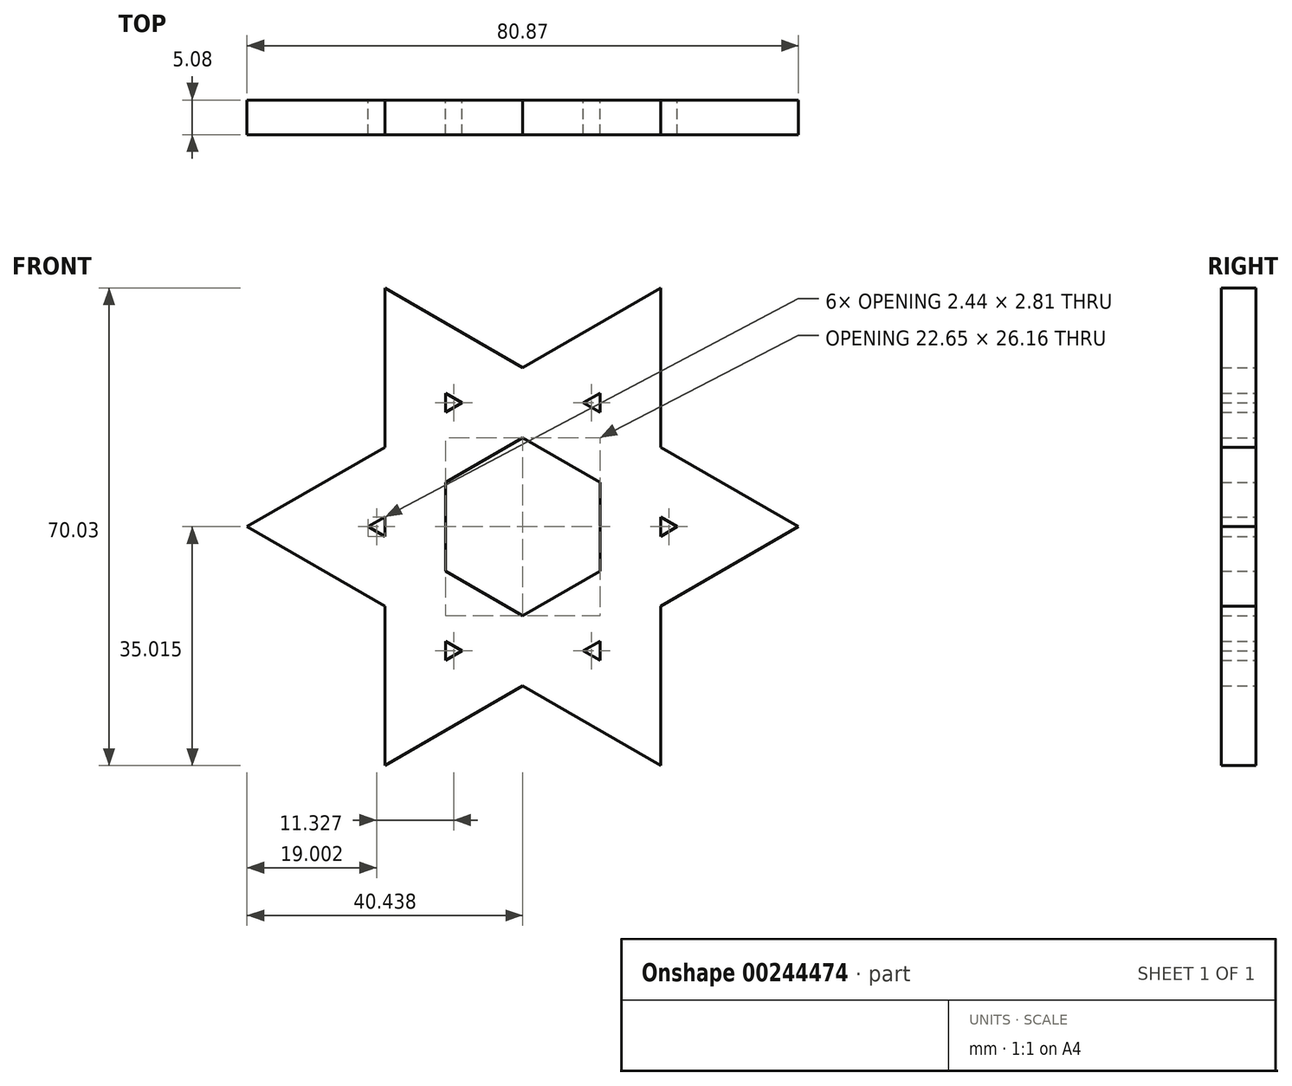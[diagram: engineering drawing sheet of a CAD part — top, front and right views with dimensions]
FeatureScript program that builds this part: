
annotation { "Feature Type Name" : "Feature", "Feature Type Description" : "" }
export const myFeature = defineFeature(function(context is Context, id is Id, definition is map)
    precondition{}
    {
        {
            var Q0;
            Q0=qCreatedBy(makeId("Front.planeOp"),FACE);
            var sketch = newSketch(context, id + "F0", { "sketchPlane" : qUnion([Q0])});
            skPoint(sketch, "E0.0.midPoint", {"position": v(-0.44, 25.15) * mm});
            skLineSegment(sketch, "E1", {"start": v(-0.44, 25.15) * mm, "end": v(-7.77, 12.45) * mm});
            skLineSegment(sketch, "E2", {"start": v(-22.21, -12.56) * mm, "end": v(-7.77, -12.7) * mm});
            skLineSegment(sketch, "E3", {"start": v(21.56, -12.95) * mm, "end": v(14.22, -0.25) * mm});
            skLineSegment(sketch, "E4", {"start": v(21.26, 12.45) * mm, "end": v(6.75, 12.45) * mm});
            skLineSegment(sketch, "E5", {"start": v(-22.44, 12.45) * mm, "end": v(-15.1, -0.25) * mm});
            skLineSegment(sketch, "E6", {"start": v(-0.59, -25.4) * mm, "end": v(6.75, -12.7) * mm});
            skLineSegment(sketch, "E7", {"start": v(-7.77, 12.45) * mm, "end": v(-15, -0.06) * mm});
            skLineSegment(sketch, "E8", {"start": v(-7.77, 12.45) * mm, "end": v(-22.44, 12.45) * mm});
            skLineSegment(sketch, "E9", {"start": v(-15, -0.06) * mm, "end": v(-22.21, -12.56) * mm});
            skLineSegment(sketch, "E10", {"start": v(-15.1, -0.25) * mm, "end": v(-7.85, -12.83) * mm});
            skLineSegment(sketch, "E11", {"start": v(6.75, 12.45) * mm, "end": v(-7.77, 12.45) * mm});
            skLineSegment(sketch, "E12", {"start": v(6.9, 12.45) * mm, "end": v(-0.44, 25.15) * mm});
            skLineSegment(sketch, "E13", {"start": v(14.22, -0.25) * mm, "end": v(6.9, 12.45) * mm});
            skLineSegment(sketch, "E14", {"start": v(14.08, 0) * mm, "end": v(21.26, 12.45) * mm});
            skLineSegment(sketch, "E15", {"start": v(6.75, -12.7) * mm, "end": v(14.08, 0) * mm});
            skLineSegment(sketch, "E16", {"start": v(6.68, -12.82) * mm, "end": v(21.56, -12.95) * mm});
            skLineSegment(sketch, "E17", {"start": v(-7.85, -12.83) * mm, "end": v(-0.59, -25.4) * mm});
            skLineSegment(sketch, "E18", {"start": v(-7.77, -12.7) * mm, "end": v(6.68, -12.82) * mm});
            skLineSegment(sketch, "E19.0", {"start": v(20.22, 95.25) * mm, "end": v(20.22, 71.9) * mm});
            skLineSegment(sketch, "E19.1", {"start": v(20.22, 25.21) * mm, "end": v(0, 36.89) * mm});
            skLineSegment(sketch, "E19.2", {"start": v(-40.43, 60.23) * mm, "end": v(-20.22, 71.9) * mm});
            skPoint(sketch, "E19.0.midPoint", {"position": v(20.22, 60.23) * mm});
            skCircle(sketch, "E20.cCircle", {"center": v(0, 60.23) * mm, "radius": 20.22 * mm, "construction": true});
            skLineSegment(sketch, "E20.0", {"start": v(-20.22, 25.21) * mm, "end": v(-20.22, 48.56) * mm});
            skLineSegment(sketch, "E20.1", {"start": v(-20.22, 95.25) * mm, "end": v(0, 83.57) * mm});
            skLineSegment(sketch, "E20.2", {"start": v(40.43, 60.23) * mm, "end": v(20.22, 48.56) * mm});
            skPoint(sketch, "E20.0.midPoint", {"position": v(-20.22, 60.23) * mm});
            skLineSegment(sketch, "E21", {"start": v(8.9, 78.44) * mm, "end": v(20.22, 71.9) * mm});
            skLineSegment(sketch, "E22", {"start": v(0, 83.57) * mm, "end": v(20.22, 95.25) * mm});
            skLineSegment(sketch, "E23", {"start": v(20.22, 71.9) * mm, "end": v(40.43, 60.23) * mm});
            skLineSegment(sketch, "E24", {"start": v(20.22, 61.64) * mm, "end": v(20.22, 48.56) * mm});
            skLineSegment(sketch, "E25", {"start": v(20.22, 48.56) * mm, "end": v(20.22, 25.21) * mm});
            skLineSegment(sketch, "E26", {"start": v(11.33, 43.43) * mm, "end": v(0, 36.89) * mm});
            skLineSegment(sketch, "E27", {"start": v(0, 36.89) * mm, "end": v(-20.22, 25.21) * mm});
            skLineSegment(sketch, "E28", {"start": v(-8.9, 42.02) * mm, "end": v(-20.22, 48.56) * mm});
            skLineSegment(sketch, "E29", {"start": v(-20.22, 48.56) * mm, "end": v(-40.43, 60.23) * mm});
            skLineSegment(sketch, "E30", {"start": v(-20.22, 58.82) * mm, "end": v(-20.22, 71.9) * mm});
            skLineSegment(sketch, "E31", {"start": v(-20.22, 71.9) * mm, "end": v(-20.22, 95.25) * mm});
            skLineSegment(sketch, "E32", {"start": v(-11.33, 77.04) * mm, "end": v(0, 83.57) * mm});
            skLineSegment(sketch, "E33.0", {"start": v(-11.33, 53.7) * mm, "end": v(-11.33, 66.77) * mm});
            skLineSegment(sketch, "E33.1", {"start": v(0, 73.3) * mm, "end": v(11.33, 66.77) * mm});
            skLineSegment(sketch, "E33.2", {"start": v(11.33, 66.77) * mm, "end": v(11.33, 53.7) * mm});
            skLineSegment(sketch, "E33.3", {"start": v(-11.33, 66.77) * mm, "end": v(0, 73.3) * mm});
            skLineSegment(sketch, "E33.4", {"start": v(11.33, 53.7) * mm, "end": v(0, 47.15) * mm});
            skLineSegment(sketch, "E33.5", {"start": v(0, 47.15) * mm, "end": v(-11.33, 53.7) * mm});
            skLineSegment(sketch, "E34", {"start": v(-8.84, 78.41) * mm, "end": v(-11.33, 79.85) * mm});
            skLineSegment(sketch, "E35", {"start": v(-11.33, 66.77) * mm, "end": v(-11.33, 79.85) * mm});
            skLineSegment(sketch, "E36", {"start": v(11.33, 66.77) * mm, "end": v(22.65, 60.23) * mm});
            skLineSegment(sketch, "E37", {"start": v(20.17, 58.8) * mm, "end": v(22.65, 60.23) * mm});
            skLineSegment(sketch, "E38", {"start": v(-20.17, 61.67) * mm, "end": v(-22.65, 60.23) * mm});
            skLineSegment(sketch, "E39", {"start": v(-11.33, 53.7) * mm, "end": v(-22.65, 60.23) * mm});
            skLineSegment(sketch, "E40", {"start": v(-11.33, 43.48) * mm, "end": v(-11.33, 40.61) * mm});
            skLineSegment(sketch, "E41", {"start": v(0, 47.15) * mm, "end": v(-11.33, 40.61) * mm});
            skLineSegment(sketch, "E42", {"start": v(8.84, 42.05) * mm, "end": v(11.33, 40.61) * mm});
            skLineSegment(sketch, "E43", {"start": v(11.33, 53.7) * mm, "end": v(11.33, 40.61) * mm});
            skLineSegment(sketch, "E44", {"start": v(0, 73.3) * mm, "end": v(11.33, 79.85) * mm});
            skLineSegment(sketch, "E45", {"start": v(11.33, 76.98) * mm, "end": v(11.33, 79.85) * mm});
            skPoint(sketch, "E46.orphan", {"position": v(15.26, 82.12) * mm});
            skPoint(sketch, "E47.orphan", {"position": v(-15.26, 82.12) * mm});
            skLineSegment(sketch, "E48.0", {"start": v(143.19, 1.7) * mm, "end": v(143.19, -21.64) * mm});
            skLineSegment(sketch, "E48.1", {"start": v(143.19, -68.33) * mm, "end": v(122.97, -56.66) * mm});
            skLineSegment(sketch, "E48.2", {"start": v(82.53, -33.31) * mm, "end": v(102.75, -21.64) * mm});
            skPoint(sketch, "E48.0.midPoint", {"position": v(143.19, -33.31) * mm});
            skCircle(sketch, "E49.cCircle", {"center": v(122.97, -33.31) * mm, "radius": 20.22 * mm, "construction": true});
            skLineSegment(sketch, "E49.0", {"start": v(102.75, -68.33) * mm, "end": v(102.75, -44.99) * mm});
            skLineSegment(sketch, "E49.1", {"start": v(102.75, 1.7) * mm, "end": v(122.97, -9.97) * mm});
            skLineSegment(sketch, "E49.2", {"start": v(163.4, -33.31) * mm, "end": v(143.19, -44.99) * mm});
            skPoint(sketch, "E49.0.midPoint", {"position": v(102.75, -33.31) * mm});
            skLineSegment(sketch, "E50", {"start": v(131.86, -15.1) * mm, "end": v(134.3, -16.5) * mm});
            skLineSegment(sketch, "E51", {"start": v(122.97, -9.97) * mm, "end": v(143.19, 1.7) * mm});
            skLineSegment(sketch, "E52", {"start": v(143.19, -21.64) * mm, "end": v(163.4, -33.31) * mm});
            skLineSegment(sketch, "E53", {"start": v(143.19, -31.9) * mm, "end": v(143.19, -34.72) * mm});
            skLineSegment(sketch, "E54", {"start": v(143.19, -44.99) * mm, "end": v(143.19, -68.33) * mm});
            skLineSegment(sketch, "E55", {"start": v(134.3, -50.12) * mm, "end": v(122.97, -56.66) * mm});
            skLineSegment(sketch, "E56", {"start": v(122.97, -56.66) * mm, "end": v(102.75, -68.33) * mm});
            skLineSegment(sketch, "E57", {"start": v(114.08, -51.53) * mm, "end": v(111.64, -50.12) * mm});
            skLineSegment(sketch, "E58", {"start": v(102.75, -44.99) * mm, "end": v(82.53, -33.31) * mm});
            skLineSegment(sketch, "E59", {"start": v(102.75, -34.72) * mm, "end": v(102.75, -31.9) * mm});
            skLineSegment(sketch, "E60", {"start": v(102.75, -21.64) * mm, "end": v(102.75, 1.7) * mm});
            skLineSegment(sketch, "E61", {"start": v(111.64, -16.5) * mm, "end": v(114.08, -15.1) * mm});
            skLineSegment(sketch, "E62.0", {"start": v(111.64, -39.85) * mm, "end": v(111.64, -26.77) * mm});
            skLineSegment(sketch, "E62.1", {"start": v(122.97, -20.24) * mm, "end": v(134.3, -26.77) * mm});
            skLineSegment(sketch, "E62.2", {"start": v(134.3, -26.77) * mm, "end": v(134.3, -39.85) * mm});
            skLineSegment(sketch, "E62.3", {"start": v(111.64, -26.77) * mm, "end": v(122.97, -20.24) * mm});
            skLineSegment(sketch, "E62.4", {"start": v(134.3, -39.85) * mm, "end": v(122.97, -46.4) * mm});
            skLineSegment(sketch, "E62.5", {"start": v(122.97, -46.4) * mm, "end": v(111.64, -39.85) * mm});
            skLineSegment(sketch, "E63", {"start": v(114.13, -15.13) * mm, "end": v(111.64, -13.7) * mm});
            skLineSegment(sketch, "E64", {"start": v(111.64, -16.57) * mm, "end": v(111.64, -13.7) * mm});
            skLineSegment(sketch, "E65", {"start": v(143.13, -31.88) * mm, "end": v(145.62, -33.31) * mm});
            skLineSegment(sketch, "E66", {"start": v(143.13, -34.75) * mm, "end": v(145.62, -33.31) * mm});
            skLineSegment(sketch, "E67", {"start": v(102.8, -31.88) * mm, "end": v(100.31, -33.31) * mm});
            skLineSegment(sketch, "E68", {"start": v(102.8, -34.75) * mm, "end": v(100.31, -33.31) * mm});
            skLineSegment(sketch, "E69", {"start": v(111.64, -50.06) * mm, "end": v(111.64, -52.93) * mm});
            skLineSegment(sketch, "E70", {"start": v(114.13, -51.5) * mm, "end": v(111.64, -52.93) * mm});
            skLineSegment(sketch, "E71", {"start": v(131.8, -51.5) * mm, "end": v(134.3, -52.93) * mm});
            skLineSegment(sketch, "E72", {"start": v(134.3, -50.06) * mm, "end": v(134.3, -52.93) * mm});
            skLineSegment(sketch, "E73", {"start": v(131.8, -15.13) * mm, "end": v(134.3, -13.7) * mm});
            skLineSegment(sketch, "E74", {"start": v(134.3, -16.57) * mm, "end": v(134.3, -13.7) * mm});
            skPoint(sketch, "E75.orphan", {"position": v(138.23, -11.42) * mm});
            skPoint(sketch, "E76.orphan", {"position": v(107.7, -11.42) * mm});
            skLineSegment(sketch, "E77.0", {"start": v(-108.48, 41.43) * mm, "end": v(-108.48, 18.09) * mm});
            skLineSegment(sketch, "E77.1", {"start": v(-108.48, -28.6) * mm, "end": v(-128.7, -16.93) * mm});
            skLineSegment(sketch, "E77.2", {"start": v(-169.14, 6.41) * mm, "end": v(-148.92, 18.09) * mm});
            skPoint(sketch, "E77.0.midPoint", {"position": v(-108.48, 6.41) * mm});
            skCircle(sketch, "E78.cCircle", {"center": v(-128.7, 6.41) * mm, "radius": 20.22 * mm, "construction": true});
            skLineSegment(sketch, "E78.0", {"start": v(-148.92, -28.6) * mm, "end": v(-148.92, -5.26) * mm});
            skLineSegment(sketch, "E78.1", {"start": v(-148.92, 41.43) * mm, "end": v(-128.7, 29.76) * mm});
            skLineSegment(sketch, "E78.2", {"start": v(-88.27, 6.41) * mm, "end": v(-108.48, -5.26) * mm});
            skPoint(sketch, "E78.0.midPoint", {"position": v(-148.92, 6.41) * mm});
            skLineSegment(sketch, "E79", {"start": v(-119.81, 24.63) * mm, "end": v(-108.48, 18.09) * mm});
            skLineSegment(sketch, "E80", {"start": v(-128.7, 29.76) * mm, "end": v(-108.48, 41.43) * mm});
            skLineSegment(sketch, "E81", {"start": v(-108.48, 18.09) * mm, "end": v(-88.27, 6.41) * mm});
            skLineSegment(sketch, "E82", {"start": v(-108.48, 7.82) * mm, "end": v(-108.48, -5.26) * mm});
            skLineSegment(sketch, "E83", {"start": v(-108.48, -5.26) * mm, "end": v(-108.48, -28.6) * mm});
            skLineSegment(sketch, "E84", {"start": v(-117.37, -10.4) * mm, "end": v(-128.7, -16.93) * mm});
            skLineSegment(sketch, "E85", {"start": v(-128.7, -16.93) * mm, "end": v(-148.92, -28.6) * mm});
            skLineSegment(sketch, "E86", {"start": v(-137.6, -11.8) * mm, "end": v(-148.92, -5.26) * mm});
            skLineSegment(sketch, "E87", {"start": v(-148.92, -5.26) * mm, "end": v(-169.14, 6.41) * mm});
            skLineSegment(sketch, "E88", {"start": v(-148.92, 5) * mm, "end": v(-148.92, 18.09) * mm});
            skLineSegment(sketch, "E89", {"start": v(-148.92, 18.09) * mm, "end": v(-148.92, 41.43) * mm});
            skLineSegment(sketch, "E90", {"start": v(-140.03, 23.22) * mm, "end": v(-128.7, 29.76) * mm});
            skLineSegment(sketch, "E91.0", {"start": v(-140.03, -0.13) * mm, "end": v(-140.03, 12.95) * mm});
            skLineSegment(sketch, "E91.1", {"start": v(-128.7, 19.5) * mm, "end": v(-117.37, 12.95) * mm});
            skLineSegment(sketch, "E91.2", {"start": v(-117.37, 12.95) * mm, "end": v(-117.37, -0.13) * mm});
            skLineSegment(sketch, "E91.3", {"start": v(-140.03, 12.95) * mm, "end": v(-128.7, 19.5) * mm});
            skLineSegment(sketch, "E91.4", {"start": v(-117.37, -0.13) * mm, "end": v(-128.7, -6.67) * mm});
            skLineSegment(sketch, "E91.5", {"start": v(-128.7, -6.67) * mm, "end": v(-140.03, -0.13) * mm});
            skLineSegment(sketch, "E92", {"start": v(-137.54, 24.6) * mm, "end": v(-140.03, 26.03) * mm});
            skLineSegment(sketch, "E93", {"start": v(-140.03, 12.95) * mm, "end": v(-140.03, 26.03) * mm});
            skLineSegment(sketch, "E94", {"start": v(-117.37, 12.95) * mm, "end": v(-106.05, 6.41) * mm});
            skLineSegment(sketch, "E95", {"start": v(-108.54, 4.98) * mm, "end": v(-106.05, 6.41) * mm});
            skLineSegment(sketch, "E96", {"start": v(-148.87, 7.85) * mm, "end": v(-151.36, 6.41) * mm});
            skLineSegment(sketch, "E97", {"start": v(-140.03, -0.13) * mm, "end": v(-151.36, 6.41) * mm});
            skLineSegment(sketch, "E98", {"start": v(-140.03, -10.33) * mm, "end": v(-140.03, -13.2) * mm});
            skLineSegment(sketch, "E99", {"start": v(-128.7, -6.67) * mm, "end": v(-140.03, -13.2) * mm});
            skLineSegment(sketch, "E100", {"start": v(-119.86, -11.77) * mm, "end": v(-117.37, -13.2) * mm});
            skLineSegment(sketch, "E101", {"start": v(-117.37, -0.13) * mm, "end": v(-117.37, -13.2) * mm});
            skLineSegment(sketch, "E102", {"start": v(-128.7, 19.5) * mm, "end": v(-117.37, 26.03) * mm});
            skLineSegment(sketch, "E103", {"start": v(-117.37, 23.16) * mm, "end": v(-117.37, 26.03) * mm});
            skPoint(sketch, "E104.orphan", {"position": v(-113.44, 28.3) * mm});
            skPoint(sketch, "E105.orphan", {"position": v(-143.96, 28.3) * mm});
            skLineSegment(sketch, "E106.0", {"start": v(-127.43, 27.56) * mm, "end": v(-111.02, 37.03) * mm});
            skLineSegment(sketch, "E106.1", {"start": v(-137.49, 21.75) * mm, "end": v(-127.43, 27.56) * mm});
            skLineSegment(sketch, "E107.0", {"start": v(-129.97, 21.7) * mm, "end": v(-114.83, 30.43) * mm});
            skLineSegment(sketch, "E108.0", {"start": v(-114.83, 24.69) * mm, "end": v(-114.83, 30.43) * mm});
            skLineSegment(sketch, "E109.0", {"start": v(-114.83, 24.69) * mm, "end": v(-111.02, 22.49) * mm});
            skLineSegment(sketch, "E110.trimOffspring", {"start": v(-111.02, 37.03) * mm, "end": v(-111.02, 22.49) * mm});
            skLineSegment(sketch, "E111.trimOffspring", {"start": v(-111.02, 19.55) * mm, "end": v(-111.02, 18.09) * mm});
            skLineSegment(sketch, "E112.trimOffspring", {"start": v(-137.49, 24.62) * mm, "end": v(-137.49, 24.69) * mm});
            skLineSegment(sketch, "E113.trimOffspring", {"start": v(-137.49, 17.35) * mm, "end": v(-129.97, 21.7) * mm});
            skLineSegment(sketch, "E114.trimOffspring", {"start": v(-137.49, 17.35) * mm, "end": v(-137.49, 21.75) * mm});
            skLineSegment(sketch, "E115.0", {"start": v(179.97, 148.6) * mm, "end": v(179.97, 125.25) * mm});
            skLineSegment(sketch, "E115.1", {"start": v(179.97, 78.56) * mm, "end": v(159.75, 90.24) * mm});
            skLineSegment(sketch, "E115.2", {"start": v(119.32, 113.58) * mm, "end": v(139.54, 125.25) * mm});
            skPoint(sketch, "E115.0.midPoint", {"position": v(179.97, 113.58) * mm});
            skCircle(sketch, "E116.cCircle", {"center": v(159.75, 113.58) * mm, "radius": 20.22 * mm, "construction": true});
            skLineSegment(sketch, "E116.0", {"start": v(139.54, 78.56) * mm, "end": v(139.54, 101.9) * mm});
            skLineSegment(sketch, "E116.1", {"start": v(139.54, 148.6) * mm, "end": v(159.75, 136.93) * mm});
            skLineSegment(sketch, "E116.2", {"start": v(200.19, 113.58) * mm, "end": v(179.97, 101.9) * mm});
            skPoint(sketch, "E116.0.midPoint", {"position": v(139.54, 113.58) * mm});
            skLineSegment(sketch, "E117", {"start": v(168.64, 131.8) * mm, "end": v(179.97, 125.25) * mm});
            skLineSegment(sketch, "E118", {"start": v(159.75, 136.93) * mm, "end": v(179.97, 148.6) * mm});
            skLineSegment(sketch, "E119", {"start": v(179.97, 125.25) * mm, "end": v(200.19, 113.58) * mm});
            skLineSegment(sketch, "E120", {"start": v(179.97, 114.99) * mm, "end": v(179.97, 101.9) * mm});
            skLineSegment(sketch, "E121", {"start": v(179.97, 101.9) * mm, "end": v(179.97, 78.56) * mm});
            skLineSegment(sketch, "E122", {"start": v(171.08, 96.78) * mm, "end": v(159.75, 90.24) * mm});
            skLineSegment(sketch, "E123", {"start": v(159.75, 90.24) * mm, "end": v(139.54, 78.56) * mm});
            skLineSegment(sketch, "E124", {"start": v(150.86, 95.37) * mm, "end": v(139.54, 101.9) * mm});
            skLineSegment(sketch, "E125", {"start": v(139.54, 101.9) * mm, "end": v(119.32, 113.58) * mm});
            skLineSegment(sketch, "E126", {"start": v(139.54, 112.17) * mm, "end": v(139.54, 125.25) * mm});
            skLineSegment(sketch, "E127", {"start": v(139.54, 125.25) * mm, "end": v(139.54, 148.6) * mm});
            skLineSegment(sketch, "E128", {"start": v(148.43, 130.39) * mm, "end": v(159.75, 136.93) * mm});
            skLineSegment(sketch, "E129.0", {"start": v(148.43, 107.04) * mm, "end": v(148.43, 120.12) * mm});
            skLineSegment(sketch, "E129.1", {"start": v(159.75, 126.66) * mm, "end": v(171.08, 120.12) * mm});
            skLineSegment(sketch, "E129.2", {"start": v(171.08, 120.12) * mm, "end": v(171.08, 107.04) * mm});
            skLineSegment(sketch, "E129.3", {"start": v(148.43, 120.12) * mm, "end": v(159.75, 126.66) * mm});
            skLineSegment(sketch, "E129.4", {"start": v(171.08, 107.04) * mm, "end": v(159.75, 100.5) * mm});
            skLineSegment(sketch, "E129.5", {"start": v(159.75, 100.5) * mm, "end": v(148.43, 107.04) * mm});
            skLineSegment(sketch, "E130", {"start": v(150.92, 131.76) * mm, "end": v(148.43, 133.2) * mm});
            skLineSegment(sketch, "E131", {"start": v(148.43, 120.12) * mm, "end": v(148.43, 133.2) * mm});
            skLineSegment(sketch, "E132", {"start": v(171.08, 120.12) * mm, "end": v(182.4, 113.58) * mm});
            skLineSegment(sketch, "E133", {"start": v(179.92, 112.14) * mm, "end": v(182.4, 113.58) * mm});
            skLineSegment(sketch, "E134", {"start": v(139.59, 115.02) * mm, "end": v(137.1, 113.58) * mm});
            skLineSegment(sketch, "E135", {"start": v(148.43, 107.04) * mm, "end": v(137.1, 113.58) * mm});
            skLineSegment(sketch, "E136", {"start": v(148.43, 96.83) * mm, "end": v(148.43, 93.96) * mm});
            skLineSegment(sketch, "E137", {"start": v(159.75, 100.5) * mm, "end": v(148.43, 93.96) * mm});
            skLineSegment(sketch, "E138", {"start": v(168.6, 95.4) * mm, "end": v(171.08, 93.96) * mm});
            skLineSegment(sketch, "E139", {"start": v(171.08, 107.04) * mm, "end": v(171.08, 93.96) * mm});
            skLineSegment(sketch, "E140", {"start": v(159.75, 126.66) * mm, "end": v(171.08, 133.2) * mm});
            skLineSegment(sketch, "E141", {"start": v(171.08, 130.33) * mm, "end": v(171.08, 133.2) * mm});
            skPoint(sketch, "E142.orphan", {"position": v(175.02, 135.47) * mm});
            skPoint(sketch, "E143.orphan", {"position": v(144.5, 135.47) * mm});
            skLineSegment(sketch, "E144.0", {"start": v(161.02, 134.73) * mm, "end": v(177.43, 144.2) * mm});
            skLineSegment(sketch, "E144.1", {"start": v(150.97, 128.92) * mm, "end": v(161.02, 134.73) * mm});
            skLineSegment(sketch, "E145.0", {"start": v(158.48, 128.86) * mm, "end": v(173.62, 137.6) * mm});
            skLineSegment(sketch, "E146.0", {"start": v(173.62, 131.85) * mm, "end": v(173.62, 137.6) * mm});
            skLineSegment(sketch, "E147.0", {"start": v(173.62, 131.85) * mm, "end": v(177.43, 129.65) * mm});
            skLineSegment(sketch, "E148.trimOffspring", {"start": v(177.43, 144.2) * mm, "end": v(177.43, 129.65) * mm});
            skLineSegment(sketch, "E149.trimOffspring", {"start": v(150.97, 131.79) * mm, "end": v(150.97, 131.85) * mm});
            skLineSegment(sketch, "E150.trimOffspring", {"start": v(150.97, 124.52) * mm, "end": v(158.48, 128.86) * mm});
            skLineSegment(sketch, "E151.trimOffspring", {"start": v(150.97, 124.52) * mm, "end": v(150.97, 128.92) * mm});
            skLineSegment(sketch, "E152.0", {"start": v(158.54, 92.43) * mm, "end": v(142.14, 82.96) * mm});
            skLineSegment(sketch, "E152.1", {"start": v(168.6, 98.24) * mm, "end": v(158.54, 92.43) * mm});
            skLineSegment(sketch, "E153.0", {"start": v(161.08, 98.3) * mm, "end": v(145.95, 89.56) * mm});
            skLineSegment(sketch, "E154.0", {"start": v(145.95, 95.3) * mm, "end": v(145.95, 89.56) * mm});
            skLineSegment(sketch, "E155.0", {"start": v(145.95, 95.3) * mm, "end": v(142.14, 97.5) * mm});
            skLineSegment(sketch, "E156.trimOffspring", {"start": v(142.14, 82.96) * mm, "end": v(142.14, 97.5) * mm});
            skLineSegment(sketch, "E157.trimOffspring", {"start": v(168.6, 102.64) * mm, "end": v(161.08, 98.3) * mm});
            skLineSegment(sketch, "E158.trimOffspring", {"start": v(168.6, 102.64) * mm, "end": v(168.6, 98.24) * mm});
            skLineSegment(sketch, "E159.0", {"start": v(177.57, 101.84) * mm, "end": v(177.57, 82.9) * mm});
            skLineSegment(sketch, "E160.0", {"start": v(173.76, 106.97) * mm, "end": v(173.76, 89.5) * mm});
            skLineSegment(sketch, "E161.0", {"start": v(168.78, 92.36) * mm, "end": v(173.76, 89.5) * mm});
            skLineSegment(sketch, "E162.0", {"start": v(168.78, 92.36) * mm, "end": v(164.97, 90.16) * mm});
            skLineSegment(sketch, "E163.trimOffspring", {"start": v(177.57, 82.9) * mm, "end": v(164.97, 90.16) * mm});
            skLineSegment(sketch, "E164.trimOffspring", {"start": v(173.76, 115.65) * mm, "end": v(173.76, 106.97) * mm});
            skLineSegment(sketch, "E165.trimOffspring", {"start": v(173.76, 115.65) * mm, "end": v(177.57, 113.45) * mm});
            skLineSegment(sketch, "E166.0", {"start": v(142.18, 125.13) * mm, "end": v(142.18, 144.08) * mm});
            skLineSegment(sketch, "E166.1", {"start": v(142.18, 113.52) * mm, "end": v(142.18, 125.13) * mm});
            skLineSegment(sketch, "E167.0", {"start": v(146, 120) * mm, "end": v(146, 137.48) * mm});
            skLineSegment(sketch, "E168.0", {"start": v(150.97, 134.6) * mm, "end": v(146, 137.48) * mm});
            skLineSegment(sketch, "E169.0", {"start": v(150.97, 134.6) * mm, "end": v(154.78, 136.8) * mm});
            skLineSegment(sketch, "E170.trimOffspring", {"start": v(142.18, 144.08) * mm, "end": v(154.78, 136.8) * mm});
            skLineSegment(sketch, "E171.trimOffspring", {"start": v(146, 111.32) * mm, "end": v(146, 120) * mm});
            skLineSegment(sketch, "E172.trimOffspring", {"start": v(146, 111.32) * mm, "end": v(142.18, 113.52) * mm});
            skLineSegment(sketch, "E173", {"start": v(177.57, 101.84) * mm, "end": v(177.57, 113.45) * mm});
            skLineSegment(sketch, "E174.0", {"start": v(141.16, 104.05) * mm, "end": v(124.75, 113.53) * mm});
            skLineSegment(sketch, "E175.0", {"start": v(147.5, 104.79) * mm, "end": v(132.37, 113.53) * mm});
            skLineSegment(sketch, "E176.0", {"start": v(137.35, 116.4) * mm, "end": v(132.37, 113.53) * mm});
            skLineSegment(sketch, "E177.0", {"start": v(137.35, 116.4) * mm, "end": v(137.35, 120.8) * mm});
            skLineSegment(sketch, "E178.trimOffspring", {"start": v(124.75, 113.53) * mm, "end": v(137.35, 120.8) * mm});
            skLineSegment(sketch, "E179.trimOffspring", {"start": v(155.02, 100.45) * mm, "end": v(147.5, 104.79) * mm});
            skLineSegment(sketch, "E180.trimOffspring", {"start": v(155.02, 100.45) * mm, "end": v(151.21, 98.25) * mm});
            skLineSegment(sketch, "E181.0", {"start": v(179.03, 123.05) * mm, "end": v(195.43, 113.58) * mm});
            skLineSegment(sketch, "E181.1", {"start": v(168.97, 128.86) * mm, "end": v(179.03, 123.05) * mm});
            skLineSegment(sketch, "E182.0", {"start": v(172.68, 122.32) * mm, "end": v(187.81, 113.58) * mm});
            skLineSegment(sketch, "E183.0", {"start": v(182.84, 110.7) * mm, "end": v(187.81, 113.58) * mm});
            skLineSegment(sketch, "E184.0", {"start": v(182.84, 110.7) * mm, "end": v(182.84, 106.3) * mm});
            skLineSegment(sketch, "E185.trimOffspring", {"start": v(195.43, 113.58) * mm, "end": v(182.84, 106.3) * mm});
            skLineSegment(sketch, "E186.trimOffspring", {"start": v(165.16, 126.66) * mm, "end": v(172.68, 122.32) * mm});
            skLineSegment(sketch, "E187.trimOffspring", {"start": v(165.16, 126.66) * mm, "end": v(168.97, 128.86) * mm});
            skLineSegment(sketch, "E188", {"start": v(141.16, 104.05) * mm, "end": v(151.21, 98.25) * mm});
            skLineSegment(sketch, "E189.0", {"start": v(286.33, 84.26) * mm, "end": v(286.33, 60.92) * mm});
            skLineSegment(sketch, "E189.1", {"start": v(286.33, 14.23) * mm, "end": v(266.11, 25.9) * mm});
            skLineSegment(sketch, "E189.2", {"start": v(225.68, 49.25) * mm, "end": v(245.9, 60.92) * mm});
            skPoint(sketch, "E189.0.midPoint", {"position": v(286.33, 49.25) * mm});
            skCircle(sketch, "E190.cCircle", {"center": v(266.11, 49.25) * mm, "radius": 20.22 * mm, "construction": true});
            skLineSegment(sketch, "E190.0", {"start": v(245.9, 14.23) * mm, "end": v(245.9, 37.57) * mm});
            skLineSegment(sketch, "E190.1", {"start": v(245.9, 84.26) * mm, "end": v(266.11, 72.6) * mm});
            skLineSegment(sketch, "E190.2", {"start": v(306.54, 49.25) * mm, "end": v(286.33, 37.57) * mm});
            skPoint(sketch, "E190.0.midPoint", {"position": v(245.9, 49.25) * mm});
            skLineSegment(sketch, "E191", {"start": v(275, 67.46) * mm, "end": v(286.33, 60.92) * mm});
            skLineSegment(sketch, "E192", {"start": v(266.11, 72.6) * mm, "end": v(286.33, 84.26) * mm});
            skLineSegment(sketch, "E193", {"start": v(286.33, 60.92) * mm, "end": v(306.54, 49.25) * mm});
            skLineSegment(sketch, "E194", {"start": v(286.33, 50.65) * mm, "end": v(286.33, 37.57) * mm});
            skLineSegment(sketch, "E195", {"start": v(286.33, 37.57) * mm, "end": v(286.33, 14.23) * mm});
            skLineSegment(sketch, "E196", {"start": v(277.44, 32.44) * mm, "end": v(266.11, 25.9) * mm});
            skLineSegment(sketch, "E197", {"start": v(266.11, 25.9) * mm, "end": v(245.9, 14.23) * mm});
            skLineSegment(sketch, "E198", {"start": v(257.22, 31.04) * mm, "end": v(245.9, 37.57) * mm});
            skLineSegment(sketch, "E199", {"start": v(245.9, 37.57) * mm, "end": v(225.68, 49.25) * mm});
            skLineSegment(sketch, "E200", {"start": v(245.9, 47.84) * mm, "end": v(245.9, 60.92) * mm});
            skLineSegment(sketch, "E201", {"start": v(245.9, 60.92) * mm, "end": v(245.9, 84.26) * mm});
            skLineSegment(sketch, "E202", {"start": v(254.78, 66.05) * mm, "end": v(266.11, 72.6) * mm});
            skLineSegment(sketch, "E203.0", {"start": v(254.78, 42.7) * mm, "end": v(254.78, 55.79) * mm});
            skLineSegment(sketch, "E203.1", {"start": v(266.11, 62.33) * mm, "end": v(277.44, 55.79) * mm});
            skLineSegment(sketch, "E203.2", {"start": v(277.44, 55.79) * mm, "end": v(277.44, 42.7) * mm});
            skLineSegment(sketch, "E203.3", {"start": v(254.78, 55.79) * mm, "end": v(266.11, 62.33) * mm});
            skLineSegment(sketch, "E203.4", {"start": v(277.44, 42.7) * mm, "end": v(266.11, 36.17) * mm});
            skLineSegment(sketch, "E203.5", {"start": v(266.11, 36.17) * mm, "end": v(254.78, 42.7) * mm});
            skLineSegment(sketch, "E204", {"start": v(257.27, 67.43) * mm, "end": v(254.78, 68.87) * mm});
            skLineSegment(sketch, "E205", {"start": v(254.78, 55.79) * mm, "end": v(254.78, 68.87) * mm});
            skLineSegment(sketch, "E206", {"start": v(277.44, 55.79) * mm, "end": v(288.76, 49.25) * mm});
            skLineSegment(sketch, "E207", {"start": v(286.28, 47.81) * mm, "end": v(288.76, 49.25) * mm});
            skLineSegment(sketch, "E208", {"start": v(245.94, 50.68) * mm, "end": v(243.46, 49.25) * mm});
            skLineSegment(sketch, "E209", {"start": v(254.78, 42.7) * mm, "end": v(243.46, 49.25) * mm});
            skLineSegment(sketch, "E210", {"start": v(254.78, 32.5) * mm, "end": v(254.78, 29.63) * mm});
            skLineSegment(sketch, "E211", {"start": v(266.11, 36.17) * mm, "end": v(254.78, 29.63) * mm});
            skLineSegment(sketch, "E212", {"start": v(274.95, 31.06) * mm, "end": v(277.44, 29.63) * mm});
            skLineSegment(sketch, "E213", {"start": v(277.44, 42.7) * mm, "end": v(277.44, 29.63) * mm});
            skLineSegment(sketch, "E214", {"start": v(266.11, 62.33) * mm, "end": v(277.44, 68.87) * mm});
            skLineSegment(sketch, "E215", {"start": v(277.44, 66) * mm, "end": v(277.44, 68.87) * mm});
            skPoint(sketch, "E216.orphan", {"position": v(281.37, 71.14) * mm});
            skPoint(sketch, "E217.orphan", {"position": v(250.85, 71.14) * mm});
            skLineSegment(sketch, "E218.0", {"start": v(267.38, 70.4) * mm, "end": v(283.79, 79.86) * mm});
            skLineSegment(sketch, "E218.1", {"start": v(257.32, 64.59) * mm, "end": v(267.38, 70.4) * mm});
            skLineSegment(sketch, "E219.0", {"start": v(264.84, 64.53) * mm, "end": v(279.98, 73.27) * mm});
            skLineSegment(sketch, "E220.0", {"start": v(279.98, 67.52) * mm, "end": v(279.98, 73.27) * mm});
            skLineSegment(sketch, "E221.0", {"start": v(279.98, 67.52) * mm, "end": v(283.79, 65.32) * mm});
            skLineSegment(sketch, "E222.trimOffspring", {"start": v(283.79, 79.86) * mm, "end": v(283.79, 65.32) * mm});
            skLineSegment(sketch, "E223.trimOffspring", {"start": v(257.32, 67.45) * mm, "end": v(257.32, 67.52) * mm});
            skLineSegment(sketch, "E224.trimOffspring", {"start": v(257.32, 60.19) * mm, "end": v(264.84, 64.53) * mm});
            skLineSegment(sketch, "E225.trimOffspring", {"start": v(257.32, 60.19) * mm, "end": v(257.32, 64.59) * mm});
            skLineSegment(sketch, "E226.0", {"start": v(264.9, 28.1) * mm, "end": v(248.5, 18.63) * mm});
            skLineSegment(sketch, "E226.1", {"start": v(274.96, 33.9) * mm, "end": v(264.9, 28.1) * mm});
            skLineSegment(sketch, "E227.0", {"start": v(267.44, 33.96) * mm, "end": v(252.3, 25.23) * mm});
            skLineSegment(sketch, "E228.0", {"start": v(252.3, 30.97) * mm, "end": v(252.3, 25.23) * mm});
            skLineSegment(sketch, "E229.0", {"start": v(252.3, 30.97) * mm, "end": v(248.5, 33.17) * mm});
            skLineSegment(sketch, "E230.trimOffspring", {"start": v(248.5, 18.63) * mm, "end": v(248.5, 33.17) * mm});
            skLineSegment(sketch, "E231.trimOffspring", {"start": v(274.96, 38.3) * mm, "end": v(267.44, 33.96) * mm});
            skLineSegment(sketch, "E232.trimOffspring", {"start": v(274.96, 38.3) * mm, "end": v(274.96, 33.9) * mm});
            skLineSegment(sketch, "E233.0", {"start": v(283.92, 37.5) * mm, "end": v(283.92, 18.56) * mm});
            skLineSegment(sketch, "E234.0", {"start": v(280.11, 42.64) * mm, "end": v(280.11, 25.16) * mm});
            skLineSegment(sketch, "E235.0", {"start": v(275.14, 28.03) * mm, "end": v(280.11, 25.16) * mm});
            skLineSegment(sketch, "E236.0", {"start": v(275.14, 28.03) * mm, "end": v(271.33, 25.83) * mm});
            skLineSegment(sketch, "E237.trimOffspring", {"start": v(283.92, 18.56) * mm, "end": v(271.33, 25.83) * mm});
            skLineSegment(sketch, "E238.trimOffspring", {"start": v(280.11, 51.32) * mm, "end": v(280.11, 42.64) * mm});
            skLineSegment(sketch, "E239.trimOffspring", {"start": v(280.11, 51.32) * mm, "end": v(283.92, 49.12) * mm});
            skLineSegment(sketch, "E240.0", {"start": v(248.54, 60.8) * mm, "end": v(248.54, 79.74) * mm});
            skLineSegment(sketch, "E240.1", {"start": v(248.54, 49.19) * mm, "end": v(248.54, 60.8) * mm});
            skLineSegment(sketch, "E241.0", {"start": v(252.35, 55.67) * mm, "end": v(252.35, 73.15) * mm});
            skLineSegment(sketch, "E242.0", {"start": v(257.33, 70.27) * mm, "end": v(252.35, 73.15) * mm});
            skLineSegment(sketch, "E243.0", {"start": v(257.33, 70.27) * mm, "end": v(261.14, 72.47) * mm});
            skLineSegment(sketch, "E244.trimOffspring", {"start": v(248.54, 79.74) * mm, "end": v(261.14, 72.47) * mm});
            skLineSegment(sketch, "E245.trimOffspring", {"start": v(252.35, 46.99) * mm, "end": v(252.35, 55.67) * mm});
            skLineSegment(sketch, "E246.trimOffspring", {"start": v(252.35, 46.99) * mm, "end": v(248.54, 49.19) * mm});
            skLineSegment(sketch, "E247", {"start": v(283.92, 37.5) * mm, "end": v(283.92, 49.12) * mm});
            skLineSegment(sketch, "E248.0", {"start": v(247.51, 39.72) * mm, "end": v(231.1, 49.2) * mm});
            skLineSegment(sketch, "E249.0", {"start": v(253.86, 40.45) * mm, "end": v(238.73, 49.2) * mm});
            skLineSegment(sketch, "E250.0", {"start": v(243.7, 52.07) * mm, "end": v(238.73, 49.2) * mm});
            skLineSegment(sketch, "E251.0", {"start": v(243.7, 52.07) * mm, "end": v(243.7, 56.47) * mm});
            skLineSegment(sketch, "E252.trimOffspring", {"start": v(231.1, 49.2) * mm, "end": v(243.7, 56.47) * mm});
            skLineSegment(sketch, "E253.trimOffspring", {"start": v(261.38, 36.11) * mm, "end": v(253.86, 40.45) * mm});
            skLineSegment(sketch, "E254.trimOffspring", {"start": v(261.38, 36.11) * mm, "end": v(257.57, 33.91) * mm});
            skLineSegment(sketch, "E255.0", {"start": v(285.38, 58.72) * mm, "end": v(301.79, 49.25) * mm});
            skLineSegment(sketch, "E255.1", {"start": v(275.32, 64.52) * mm, "end": v(285.38, 58.72) * mm});
            skLineSegment(sketch, "E256.0", {"start": v(279.03, 57.98) * mm, "end": v(294.17, 49.25) * mm});
            skLineSegment(sketch, "E257.0", {"start": v(289.2, 46.37) * mm, "end": v(294.17, 49.25) * mm});
            skLineSegment(sketch, "E258.0", {"start": v(289.2, 46.37) * mm, "end": v(289.2, 41.97) * mm});
            skLineSegment(sketch, "E259.trimOffspring", {"start": v(301.79, 49.25) * mm, "end": v(289.2, 41.97) * mm});
            skLineSegment(sketch, "E260.trimOffspring", {"start": v(271.51, 62.32) * mm, "end": v(279.03, 57.98) * mm});
            skLineSegment(sketch, "E261.trimOffspring", {"start": v(271.51, 62.32) * mm, "end": v(275.32, 64.52) * mm});
            skLineSegment(sketch, "E262", {"start": v(247.51, 39.72) * mm, "end": v(257.57, 33.91) * mm});
            skSolve(sketch);
        }
        {
            var Q0;
            Q0=makeQuery(id+"F0.imprint","IMPRINT",FACE,{"disambiguationData":[TD([[makeQuery(id+"F0.imprint","IMPRINT",EDGE,{"derivedFrom":sQuery(id+"F0.wireOp",EDGE,"E48.0")}),-1.0]])]});
            extrude(context, id + "F1", {"entities" : qUnion([Q0]), "depth" : 5.08 * mm});
        }
    });
